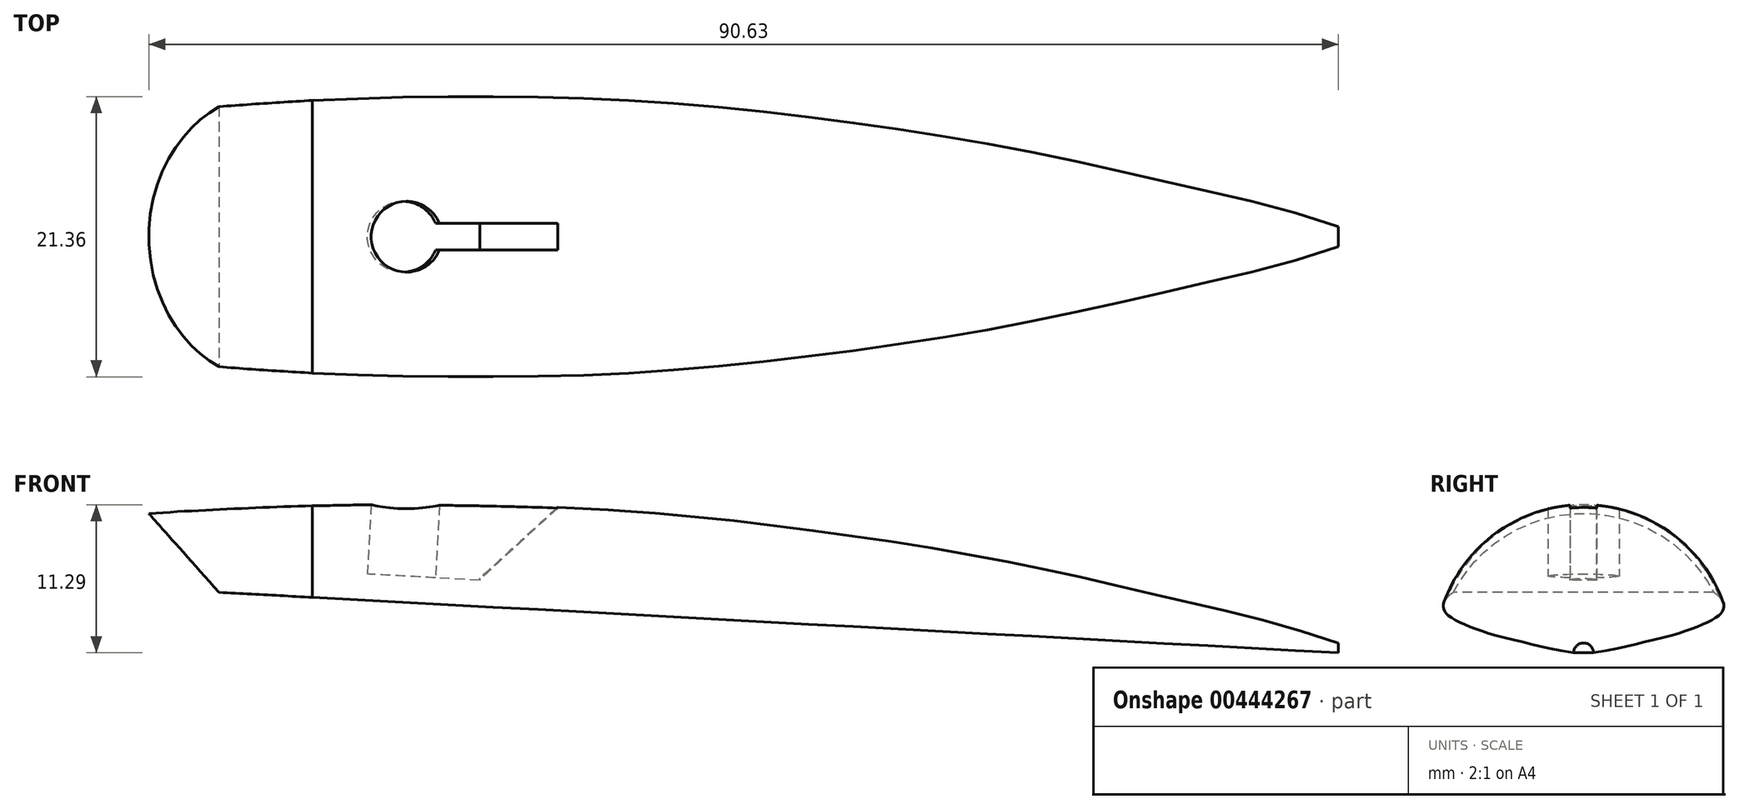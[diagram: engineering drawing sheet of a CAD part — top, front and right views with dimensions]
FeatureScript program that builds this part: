
annotation { "Feature Type Name" : "Feature", "Feature Type Description" : "" }
export const myFeature = defineFeature(function(context is Context, id is Id, definition is map)
    precondition{}
    {
        {
            var Q0;
            Q0=qCreatedBy(makeId("Top.planeOp"),FACE);
            var sketch = newSketch(context, id + "F0", { "sketchPlane" : qUnion([Q0])});
            skFitSpline(sketch, "E0", {"points": [v(50.74, 0.76) * mm, v(40.36, 3.6) * mm, v(27.98, 6.45) * mm, v(13.03, 9.02) * mm, v(-1.08, 10.63) * mm, v(-11.73, 11.19) * mm, v(-22.12, 11.3) * mm, v(-27.42, 11.23) * mm], "startDerivative": vector(-105.08, 35.47) * mm, "endDerivative": vector(-52.2, -0.15) * mm});
            skLineSegment(sketch, "E1", {"start": v(0, 0) * mm, "end": v(-76.2, 0) * mm});
            skFitSpline(sketch, "E2.MirrorCS", {"points": [v(50.74, -0.76) * mm, v(40.36, -3.6) * mm, v(27.98, -6.45) * mm, v(13.03, -9.02) * mm, v(-1.08, -10.63) * mm, v(-11.73, -11.19) * mm, v(-22.12, -11.3) * mm, v(-27.42, -11.23) * mm], "startDerivative": vector(-105.08, -35.47) * mm, "endDerivative": vector(-52.2, 0.15) * mm});
            skLineSegment(sketch, "E3", {"start": v(50.74, 0.76) * mm, "end": v(50.74, -0.76) * mm});
            skLineSegment(sketch, "E4", {"start": v(-27.42, 11.23) * mm, "end": v(-27.42, -11.23) * mm});
            skFitSpline(sketch, "E5", {"points": [v(-27.42, -11.23) * mm, v(-50.83, -9.56) * mm], "startDerivative": vector(-27.1, 0.96) * mm, "endDerivative": vector(-25.61, 3.15) * mm});
            skLineSegment(sketch, "E6", {"start": v(-27.42, 0) * mm, "end": v(50.74, 0) * mm});
            skFitSpline(sketch, "E7.MirrorCS", {"points": [v(-27.42, 11.23) * mm, v(-50.83, 9.56) * mm], "startDerivative": vector(-27.1, -0.96) * mm, "endDerivative": vector(-25.61, -3.15) * mm});
            skLineSegment(sketch, "E8", {"start": v(-50.83, -9.56) * mm, "end": v(-50.83, 9.56) * mm});
            skSolve(sketch);
        }
        {
            var Q0;
            {var subQ5=sQuery(id+"F0.wireOp",EDGE,"E0");Q0=makeQuery(id+"F0.imprint","IMPRINT",FACE,{"disambiguationData":[TD([[makeQuery(id+"F0.imprint","IMPRINT",EDGE,{"derivedFrom":subQ5}),1.0]])]});}
            var Q1;
            {var subQ5=sQuery(id+"F0.wireOp",EDGE,"E7.MirrorCS");Q1=makeQuery(id+"F0.imprint","IMPRINT",FACE,{"disambiguationData":[TD([[makeQuery(id+"F0.imprint","IMPRINT",EDGE,{"derivedFrom":subQ5}),1.0]])]});}
            var Q2;
            Q2=sQuery(id+"F0.wireOp",EDGE,"E1");
            revolve(context, id + "F1", {"entities" : qUnion([Q0, Q1]), "axis" : qUnion([Q2]), "revolveType" : RevolveType.FULL});
        }
        {
            var Q0;
            Q0=qCreatedBy(makeId("Front.planeOp"),FACE);
            var sketch = newSketch(context, id + "F2", { "sketchPlane" : qUnion([Q0])});
            skLineSegment(sketch, "E9.0", {"start": v(-50.83, 9.56) * mm, "end": v(-50.83, -9.56) * mm});
            skLineSegment(sketch, "E10", {"start": v(-50.83, -9.56) * mm, "end": v(-34.7, 4.79) * mm});
            skLineSegment(sketch, "E11", {"start": v(-34.7, 4.79) * mm, "end": v(-39.93, 10.67) * mm});
            skFitSpline(sketch, "E12", {"points": [v(-39.93, 10.67) * mm, v(-50.83, 9.56) * mm], "startDerivative": vector(-10.94, -0.63) * mm, "endDerivative": vector(-11.09, -1.8) * mm});
            skSolve(sketch);
        }
        {
            var Q0;
            Q0=makeQuery(id+"F2.imprint","IMPRINT",FACE,{"disambiguationData":[TD([[makeQuery(id+"F2.imprint","IMPRINT",EDGE,{"derivedFrom":sQuery(id+"F2.wireOp",EDGE,"E9.0")}),1.0]])]});
            extrude(context, id + "F3", {"entities" : qUnion([Q0]), "operationType" : NewBodyOperationType.REMOVE, "endBound" : BoundingType.SYMMETRIC, "oppositeDirection" : true, "depth" : 25.4 * mm});
        }
        {
            var Q0;
            Q0=makeQuery(id+"F3.boolean.opBoolean","COPY",FACE,{"derivedFrom":makeQuery(id+"F3.opExtrude","SWEPT_FACE",FACE,{"disambiguationData":[OSD([sQuery(id+"F2.wireOp",EDGE,"E11")])]})});
            var sketch = newSketch(context, id + "F4", { "sketchPlane" : qUnion([Q0])});
            skFitSpline(sketch, "E13", {"points": [v(10.62, 26.64) * mm, v(-10.64, 26.64) * mm], "startDerivative": vector(-14.87, -5.24) * mm, "endDerivative": vector(-14.04, 5.24) * mm});
            skLineSegment(sketch, "E14", {"start": v(-10.64, 26.64) * mm, "end": v(10.62, 26.64) * mm});
            skSolve(sketch);
        }
        {
            var Q0;
            {var subQ0=sQuery(id+"F4.wireOp",EDGE,"E13");Q0=makeQuery(id+"F4.imprint","IMPRINT",FACE,{"disambiguationData":[TD([[makeQuery(id+"F4.imprint","IMPRINT",EDGE,{"derivedFrom":subQ0}),-1.0]])]});}
            extrude(context, id + "F5", {"entities" : qUnion([Q0]), "operationType" : NewBodyOperationType.REMOVE, "endBound" : BoundingType.THROUGH_ALL, "depth" : 25.4 * mm});
        }
        {
            var Q0;
            Q0=makeQuery(id+"F3.boolean.opBoolean","COPY",FACE,{"derivedFrom":makeQuery(id+"F3.opExtrude","SWEPT_FACE",FACE,{"disambiguationData":[OSD([sQuery(id+"F2.wireOp",EDGE,"E10")])]})});
            var sketch = newSketch(context, id + "F6", { "sketchPlane" : qUnion([Q0])});
            skLineSegment(sketch, "E15", {"start": v(-21.97, 0) * mm, "end": v(-28.83, 0) * mm, "construction": true});
            skCircle(sketch, "E16", {"center": v(-28.83, 0) * mm, "radius": 1 * mm});
            skSolve(sketch);
        }
        {
            var Q0;
            Q0=makeQuery(id+"F6.imprint","IMPRINT",FACE,{"disambiguationData":[TD([[makeQuery(id+"F6.imprint","IMPRINT",EDGE,{"derivedFrom":sQuery(id+"F6.wireOp",EDGE,"E16")}),1.0]])]});
            extrude(context, id + "F7", {"entities" : qUnion([Q0]), "operationType" : NewBodyOperationType.REMOVE, "oppositeDirection" : true, "depth" : 25.4 * mm});
        }
        {
            var Q0;
            Q0=makeQuery(id+"F7.boolean.opBoolean","INTERSECT",EDGE,{"derivedFrom":[makeQuery(id+"F5.boolean.opBoolean","COPY",FACE,{"derivedFrom":makeQuery(id+"F5.opExtrude","SWEPT_FACE",FACE,{"disambiguationData":[OSD([sQuery(id+"F4.wireOp",EDGE,"E13")])]})}),makeQuery(id+"F7.opExtrude","SWEPT_FACE",FACE,{"disambiguationData":[OSD([sQuery(id+"F6.wireOp",EDGE,"E16")])]})]});
            fillet(context, id + "F8", {"entities" : qUnion([Q0]), "radius" : 2 * mm, "tangentPropagation" : true, "allowEdgeOverflow" : false});
        }
        {
            var Q0;
            Q0=makeQuery(id+"F7.boolean.opBoolean","INTERSECT",EDGE,{"derivedFrom":[makeQuery(id+"F1.opRevolve","SWEPT_FACE",FACE,{"disambiguationData":[OSD([sQuery(id+"F0.wireOp",EDGE,"E7.MirrorCS")])]}),makeQuery(id+"F7.opExtrude","SWEPT_FACE",FACE,{"disambiguationData":[OSD([sQuery(id+"F6.wireOp",EDGE,"E16")])]})]});
            var Q1;
            Q1=makeQuery(id+"F7.boolean.opBoolean","INTERSECT",EDGE,{"derivedFrom":[makeQuery(id+"F1.opRevolve","SWEPT_FACE",FACE,{"disambiguationData":[OSD([sQuery(id+"F0.wireOp",EDGE,"E0")])]}),makeQuery(id+"F7.opExtrude","SWEPT_FACE",FACE,{"disambiguationData":[OSD([sQuery(id+"F6.wireOp",EDGE,"E16")])]})]});
            fillet(context, id + "F9", {"entities" : qUnion([Q0, Q1]), "radius" : 2 * mm, "tangentPropagation" : true, "allowEdgeOverflow" : false});
        }
        {
            var Q0;
            Q0=qCreatedBy(makeId("Front.planeOp"),FACE);
            var sketch = newSketch(context, id + "F10", { "sketchPlane" : qUnion([Q0])});
            skFitSpline(sketch, "E17.0", {"points": [v(-34.7, 4.79) * mm, v(-34.12, 4.14) * mm, v(-33.83, 3.82) * mm, v(-33.83, 3.81) * mm]});
            skPoint(sketch, "E18", {"position": v(-34.55, 4.62) * mm});
            skLineSegment(sketch, "E19", {"start": v(-34.55, 4.62) * mm, "end": v(50.9, 0) * mm});
            skLineSegment(sketch, "E20", {"start": v(-24.57, 16.63) * mm, "end": v(-45.81, 12.1) * mm});
            skLineSegment(sketch, "E21", {"start": v(-45.81, 12.1) * mm, "end": v(-34.55, 4.62) * mm});
            skLineSegment(sketch, "E22", {"start": v(50.9, 0) * mm, "end": v(55.75, 11.19) * mm});
            skLineSegment(sketch, "E23", {"start": v(55.75, 11.19) * mm, "end": v(-24.57, 16.63) * mm});
            skLineSegment(sketch, "E24", {"start": v(50.9, 0) * mm, "end": v(57.12, -13.7) * mm});
            skLineSegment(sketch, "E25", {"start": v(57.12, -13.7) * mm, "end": v(-52.13, -12.87) * mm});
            skLineSegment(sketch, "E26", {"start": v(-52.13, -12.87) * mm, "end": v(-52.86, -5.28) * mm});
            skLineSegment(sketch, "E27", {"start": v(-52.86, -5.28) * mm, "end": v(-34.7, 4.79) * mm});
            skSolve(sketch);
        }
        {
            var Q0;
            {var subQ1=sQuery(id+"F10.wireOp",EDGE,"E19");Q0=makeQuery(id+"F10.imprint","IMPRINT",FACE,{"disambiguationData":[TD([[makeQuery(id+"F10.imprint","IMPRINT",EDGE,{"derivedFrom":subQ1}),-1.0]])]});}
            extrude(context, id + "F11", {"entities" : qUnion([Q0]), "operationType" : NewBodyOperationType.REMOVE, "endBound" : BoundingType.SYMMETRIC, "oppositeDirection" : true, "depth" : 25.4 * mm});
        }
        {
            var Q0;
            Q0=makeQuery(id+"F11.boolean.opBoolean","COPY",FACE,{"derivedFrom":makeQuery(id+"F11.opExtrude","SWEPT_FACE",FACE,{"disambiguationData":[OSD([sQuery(id+"F10.wireOp",EDGE,"E19")])]})});
            var sketch = newSketch(context, id + "F12", { "sketchPlane" : qUnion([Q0])});
            skLineSegment(sketch, "E28", {"start": v(0, 0) * mm, "end": v(-20.83, 0) * mm, "construction": true});
            skCircle(sketch, "E29", {"center": v(-20.83, 0) * mm, "radius": 2.7 * mm});
            skSolve(sketch);
        }
        {
            var Q0;
            Q0=makeQuery(id+"F12.imprint","IMPRINT",FACE,{"disambiguationData":[TD([[makeQuery(id+"F12.imprint","IMPRINT",EDGE,{"derivedFrom":sQuery(id+"F12.wireOp",EDGE,"E29")}),1.0]])]});
            extrude(context, id + "F13", {"entities" : qUnion([Q0]), "operationType" : NewBodyOperationType.REMOVE, "endBound" : BoundingType.THROUGH_ALL, "oppositeDirection" : true, "depth" : 25.4 * mm});
        }
        {
            var Q0;
            Q0=makeQuery(id+"F12.imprint","IMPRINT",FACE,{"disambiguationData":[TD([[makeQuery(id+"F12.imprint","IMPRINT",EDGE,{"derivedFrom":sQuery(id+"F12.wireOp",EDGE,"E29")}),1.0]])]});
            extrude(context, id + "F14", {"entities" : qUnion([Q0]), "operationType" : NewBodyOperationType.ADD, "oppositeDirection" : true, "depth" : 2 * mm});
        }
        {
            var Q0;
            Q0=makeQuery(id+"F14.opExtrude","CAP_FACE",FACE,{"disambiguationData":[OSD([sQuery(id+"F12.wireOp",EDGE,"E29")])],"isStart":false});
            var sketch = newSketch(context, id + "F15", { "sketchPlane" : qUnion([Q0])});
            skCircle(sketch, "E30.0", {"center": v(-20.83, 0) * mm, "radius": 2.7 * mm});
            skLineSegment(sketch, "E31.bottom", {"start": v(-14.95, 1.02) * mm, "end": v(-21.3, 1.02) * mm});
            skLineSegment(sketch, "E31.top", {"start": v(-14.95, -1.02) * mm, "end": v(-21.3, -1.02) * mm});
            skLineSegment(sketch, "E31.left", {"start": v(-14.95, 1.02) * mm, "end": v(-14.95, -1.02) * mm});
            skLineSegment(sketch, "E31.right", {"start": v(-21.3, 1.02) * mm, "end": v(-21.3, -1.02) * mm});
            skPoint(sketch, "E31.middle", {"position": v(-18.13, 0) * mm});
            skSolve(sketch);
        }
        {
            var Q0;
            {var subQ5=sQuery(id+"F15.wireOp",EDGE,"E31.right");Q0=makeQuery(id+"F15.imprint","IMPRINT",FACE,{"disambiguationData":[TD([[makeQuery(id+"F15.imprint","IMPRINT",EDGE,{"derivedFrom":subQ5}),1.0]])]});}
            var Q1;
            {var subQ5=sQuery(id+"F15.wireOp",EDGE,"E31.left");Q1=makeQuery(id+"F15.imprint","IMPRINT",FACE,{"disambiguationData":[TD([[makeQuery(id+"F15.imprint","IMPRINT",EDGE,{"derivedFrom":subQ5}),-1.0]])]});}
            extrude(context, id + "F16", {"entities" : qUnion([Q0, Q1]), "operationType" : NewBodyOperationType.REMOVE, "depth" : 25.4 * mm});
        }
        {
            var Q0;
            Q0=makeQuery(id+"F16.boolean.opBoolean","INTERSECT",EDGE,{"derivedFrom":[makeQuery(id+"F1.opRevolve","SWEPT_FACE",FACE,{"disambiguationData":[OSD([sQuery(id+"F0.wireOp",EDGE,"E0")])]}),makeQuery(id+"F16.opExtrude","SWEPT_FACE",FACE,{"disambiguationData":[OSD([sQuery(id+"F15.wireOp",EDGE,"E31.left")])]})]});
            chamfer(context, id + "F17", {"entities" : qUnion([Q0]), "width" : 5.7 * mm, "tangentPropagation" : true});
        }
    });
